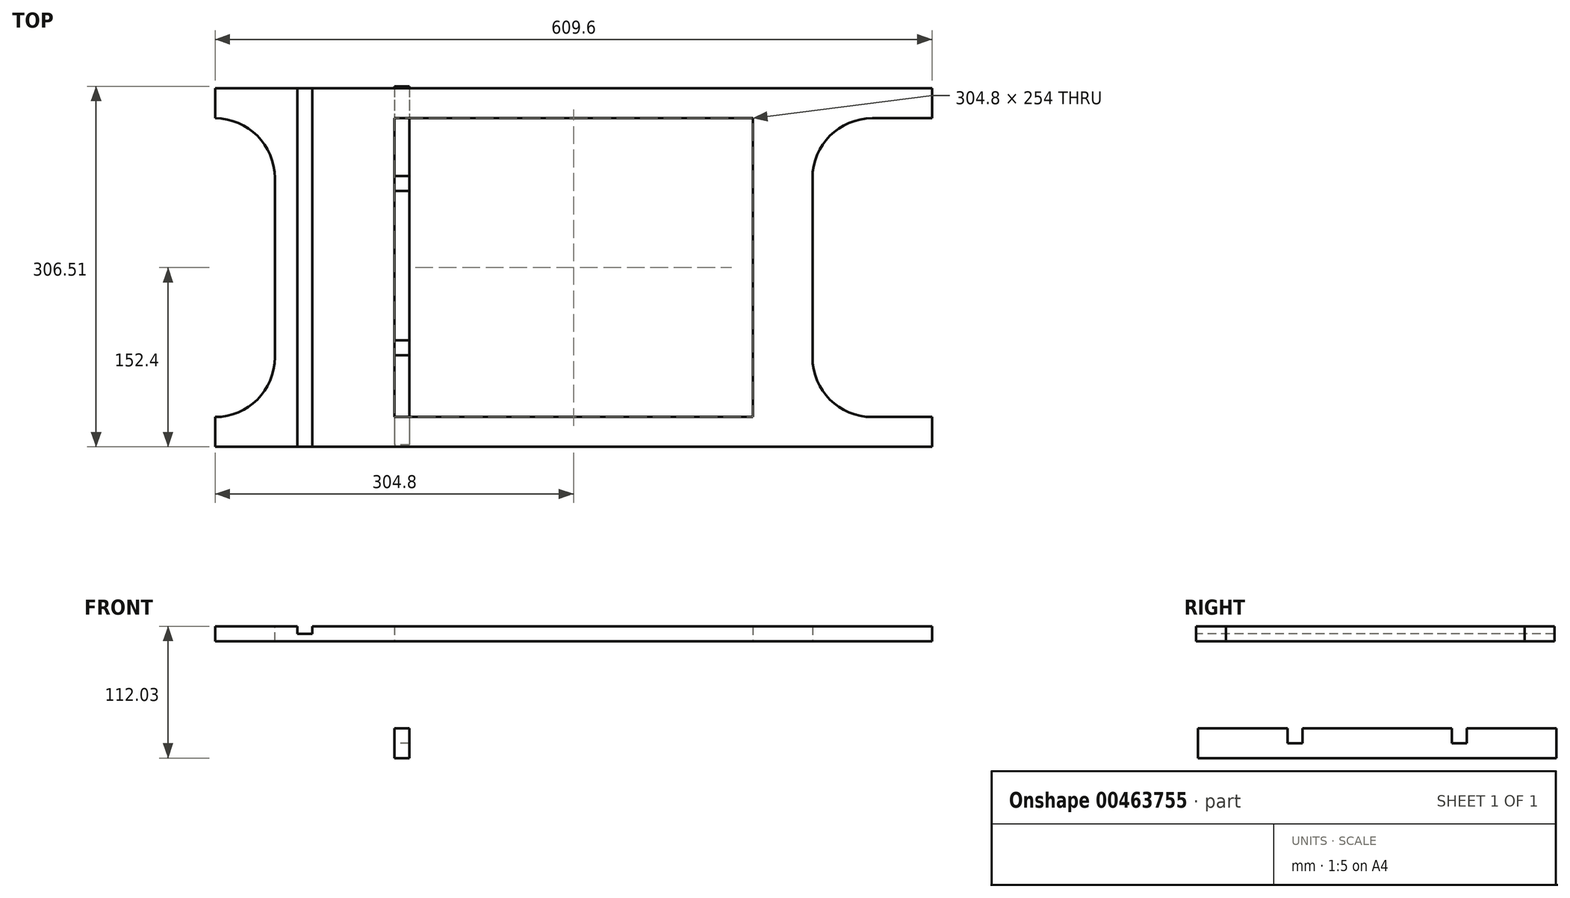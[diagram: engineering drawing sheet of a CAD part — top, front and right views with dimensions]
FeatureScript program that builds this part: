
annotation { "Feature Type Name" : "Feature", "Feature Type Description" : "" }
export const myFeature = defineFeature(function(context is Context, id is Id, definition is map)
    precondition{}
    {
        {
            var Q0;
            Q0=qCreatedBy(makeId("Top.planeOp"),FACE);
            var sketch = newSketch(context, id + "F0", { "sketchPlane" : qUnion([Q0])});
            skLineSegment(sketch, "E0.bottom", {"start": v(304.8, 152.4) * mm, "end": v(-304.8, 152.4) * mm});
            skLineSegment(sketch, "E0.top", {"start": v(304.8, -152.4) * mm, "end": v(-304.8, -152.4) * mm});
            skLineSegment(sketch, "E0.left", {"start": v(304.8, 152.4) * mm, "end": v(304.8, -152.4) * mm});
            skLineSegment(sketch, "E0.right", {"start": v(-304.8, 152.4) * mm, "end": v(-304.8, -152.4) * mm});
            skPoint(sketch, "E0.middle", {"position": v(0, 0) * mm});
            skLineSegment(sketch, "E1.bottom", {"start": v(152.4, 127) * mm, "end": v(-152.4, 127) * mm});
            skLineSegment(sketch, "E1.top", {"start": v(152.4, -127) * mm, "end": v(-152.4, -127) * mm});
            skLineSegment(sketch, "E1.left", {"start": v(152.4, 127) * mm, "end": v(152.4, -127) * mm});
            skLineSegment(sketch, "E1.right", {"start": v(-152.4, 127) * mm, "end": v(-152.4, -127) * mm});
            skLineSegment(sketch, "E2.bottom", {"start": v(304.8, 127) * mm, "end": v(203.2, 127) * mm});
            skLineSegment(sketch, "E2.top", {"start": v(304.8, -127) * mm, "end": v(203.2, -127) * mm});
            skLineSegment(sketch, "E2.left", {"start": v(304.8, 127) * mm, "end": v(304.8, -127) * mm});
            skLineSegment(sketch, "E2.right", {"start": v(203.2, 127) * mm, "end": v(203.2, -127) * mm});
            skSolve(sketch);
        }
        {
            var Q0;
            {var subQ1=sQuery(id+"F0.wireOp",EDGE,"E0.bottom");Q0=makeQuery(id+"F0.imprint","IMPRINT",FACE,{"disambiguationData":[TD([[makeQuery(id+"F0.imprint","IMPRINT",EDGE,{"derivedFrom":subQ1}),1.0]])]});}
            extrude(context, id + "F1", {"entities" : qUnion([Q0]), "depth" : 12.7 * mm});
        }
        {
            var Q0;
            Q0=makeQuery(id+"F1.opExtrude","CAP_FACE",FACE,{"disambiguationData":[OSD([sQuery(id+"F0.wireOp",EDGE,"E0.bottom"),sQuery(id+"F0.wireOp",EDGE,"E0.top"),sQuery(id+"F0.wireOp",EDGE,"E0.left"),sQuery(id+"F0.wireOp",EDGE,"E0.right"),sQuery(id+"F0.wireOp",EDGE,"E1.bottom"),sQuery(id+"F0.wireOp",EDGE,"E1.top"),sQuery(id+"F0.wireOp",EDGE,"E1.left"),sQuery(id+"F0.wireOp",EDGE,"E1.right"),sQuery(id+"F0.wireOp",EDGE,"E2.bottom"),sQuery(id+"F0.wireOp",EDGE,"E2.top"),sQuery(id+"F0.wireOp",EDGE,"E2.right")])],"isStart":false});
            var sketch = newSketch(context, id + "F2", { "sketchPlane" : qUnion([Q0])});
            skLineSegment(sketch, "E3.bottom", {"start": v(-234.95, 152.4) * mm, "end": v(-222.25, 152.4) * mm});
            skLineSegment(sketch, "E3.top", {"start": v(-234.95, -152.4) * mm, "end": v(-222.25, -152.4) * mm});
            skLineSegment(sketch, "E3.left", {"start": v(-234.95, 152.4) * mm, "end": v(-234.95, -152.4) * mm});
            skLineSegment(sketch, "E3.right", {"start": v(-222.25, 152.4) * mm, "end": v(-222.25, -152.4) * mm});
            skLineSegment(sketch, "E4", {"start": v(-152.4, 127) * mm, "end": v(-304.8, 127) * mm, "construction": true});
            skSolve(sketch);
        }
        {
            var Q0;
            Q0=makeQuery(id+"F2.imprint","IMPRINT",FACE,{"disambiguationData":[TD([[makeQuery(id+"F2.imprint","IMPRINT",EDGE,{"derivedFrom":sQuery(id+"F2.wireOp",EDGE,"E3.bottom")}),1.0]])]});
            extrude(context, id + "F3", {"entities" : qUnion([Q0]), "operationType" : NewBodyOperationType.REMOVE, "oppositeDirection" : true, "depth" : 6.35 * mm});
        }
        {
            var Q0;
            Q0=makeQuery(id+"F1.opExtrude","SWEPT_EDGE",EDGE,{"disambiguationData":[OSD([sQuery(id+"F0.wireOp",EDGE,"E2.top"),sQuery(id+"F0.wireOp",EDGE,"E2.right")])]});
            var Q1;
            Q1=makeQuery(id+"F1.opExtrude","SWEPT_EDGE",EDGE,{"disambiguationData":[OSD([sQuery(id+"F0.wireOp",EDGE,"E2.bottom"),sQuery(id+"F0.wireOp",EDGE,"E2.right")])]});
            fillet(context, id + "F4", {"entities" : qUnion([Q0, Q1]), "radius" : 50.8 * mm, "tangentPropagation" : true, "allowEdgeOverflow" : false});
        }
        {
            var Q0;
            {var subQ0=sQuery(id+"F0.wireOp",EDGE,"E0.bottom");var subQ1=sQuery(id+"F0.wireOp",EDGE,"E0.top");var subQ2=sQuery(id+"F0.wireOp",EDGE,"E0.right");Q0=makeQuery(id+"F3.boolean.opBoolean","SPLIT",FACE,{"disambiguationData":[TD([makeQuery(id+"F1.opExtrude","SWEPT_FACE",FACE,{"disambiguationData":[OSD([subQ2])]})])],"derivedFrom":makeQuery(id+"F1.opExtrude","CAP_FACE",FACE,{"disambiguationData":[OSD([subQ0,subQ1,sQuery(id+"F0.wireOp",EDGE,"E0.left"),subQ2,sQuery(id+"F0.wireOp",EDGE,"E1.bottom"),sQuery(id+"F0.wireOp",EDGE,"E1.top"),sQuery(id+"F0.wireOp",EDGE,"E1.left"),sQuery(id+"F0.wireOp",EDGE,"E1.right"),sQuery(id+"F0.wireOp",EDGE,"E2.bottom"),sQuery(id+"F0.wireOp",EDGE,"E2.top"),sQuery(id+"F0.wireOp",EDGE,"E2.right")])],"isStart":false})});}
            var sketch = newSketch(context, id + "F5", { "sketchPlane" : qUnion([Q0])});
            skLineSegment(sketch, "E5.bottom", {"start": v(-304.8, 127) * mm, "end": v(-254, 127) * mm});
            skLineSegment(sketch, "E5.top", {"start": v(-304.8, -127) * mm, "end": v(-254, -127) * mm});
            skLineSegment(sketch, "E5.left", {"start": v(-304.8, 127) * mm, "end": v(-304.8, -127) * mm});
            skLineSegment(sketch, "E5.right", {"start": v(-254, 127) * mm, "end": v(-254, -127) * mm});
            skSolve(sketch);
        }
        {
            var Q0;
            Q0=makeQuery(id+"F5.imprint","IMPRINT",FACE,{"disambiguationData":[TD([[makeQuery(id+"F5.imprint","IMPRINT",EDGE,{"derivedFrom":sQuery(id+"F5.wireOp",EDGE,"E5.bottom")}),-1.0]])]});
            extrude(context, id + "F6", {"entities" : qUnion([Q0]), "operationType" : NewBodyOperationType.REMOVE, "oppositeDirection" : true, "depth" : 12.7 * mm});
        }
        {
            var Q0;
            Q0=makeQuery(id+"F6.boolean.opBoolean","COPY",EDGE,{"derivedFrom":makeQuery(id+"F6.opExtrude","SWEPT_EDGE",EDGE,{"disambiguationData":[OSD([sQuery(id+"F5.wireOp",EDGE,"E5.bottom"),sQuery(id+"F5.wireOp",EDGE,"E5.right")])]})});
            var Q1;
            Q1=makeQuery(id+"F6.boolean.opBoolean","COPY",EDGE,{"derivedFrom":makeQuery(id+"F6.opExtrude","SWEPT_EDGE",EDGE,{"disambiguationData":[OSD([sQuery(id+"F5.wireOp",EDGE,"E5.top"),sQuery(id+"F5.wireOp",EDGE,"E5.right")])]})});
            fillet(context, id + "F7", {"entities" : qUnion([Q0, Q1]), "radius" : 50.8 * mm, "tangentPropagation" : true, "allowEdgeOverflow" : false});
        }
        {
            var Q0;
            Q0=makeQuery(id+"F1.opExtrude","SWEPT_FACE",FACE,{"disambiguationData":[OSD([sQuery(id+"F0.wireOp",EDGE,"E1.right")])]});
            var sketch = newSketch(context, id + "F8", { "sketchPlane" : qUnion([Q0])});
            skLineSegment(sketch, "E6.bottom", {"start": v(154.1, -73.93) * mm, "end": v(-150.7, -73.93) * mm});
            skLineSegment(sketch, "E6.top", {"start": v(154.1, -99.33) * mm, "end": v(-150.7, -99.33) * mm});
            skLineSegment(sketch, "E6.left", {"start": v(154.1, -73.93) * mm, "end": v(154.1, -99.33) * mm});
            skLineSegment(sketch, "E6.right", {"start": v(-150.7, -73.93) * mm, "end": v(-150.7, -99.33) * mm});
            skLineSegment(sketch, "E7.bottom", {"start": v(77.9, -73.93) * mm, "end": v(65.2, -73.93) * mm});
            skLineSegment(sketch, "E7.top", {"start": v(77.9, -86.63) * mm, "end": v(65.2, -86.63) * mm});
            skLineSegment(sketch, "E7.left", {"start": v(77.9, -73.93) * mm, "end": v(77.9, -86.63) * mm});
            skLineSegment(sketch, "E7.right", {"start": v(65.2, -73.93) * mm, "end": v(65.2, -86.63) * mm});
            skPoint(sketch, "E8.oppositeSnap0", {"position": v(-150.7, -86.63) * mm});
            skLineSegment(sketch, "E8.bottom", {"start": v(-61.8, -73.93) * mm, "end": v(-74.5, -73.93) * mm});
            skLineSegment(sketch, "E8.top", {"start": v(-61.8, -86.63) * mm, "end": v(-74.5, -86.63) * mm});
            skLineSegment(sketch, "E8.left", {"start": v(-61.8, -73.93) * mm, "end": v(-61.8, -86.63) * mm});
            skLineSegment(sketch, "E8.right", {"start": v(-74.5, -73.93) * mm, "end": v(-74.5, -86.63) * mm});
            skSolve(sketch);
        }
        {
            var Q0;
            Q0=makeQuery(id+"F8.imprint","IMPRINT",FACE,{"disambiguationData":[TD([[makeQuery(id+"F8.imprint","IMPRINT",EDGE,{"derivedFrom":sQuery(id+"F8.wireOp",EDGE,"E6.top")}),-1.0]])]});
            extrude(context, id + "F9", {"entities" : qUnion([Q0]), "operationType" : NewBodyOperationType.ADD, "depth" : 12.7 * mm});
        }
    });
